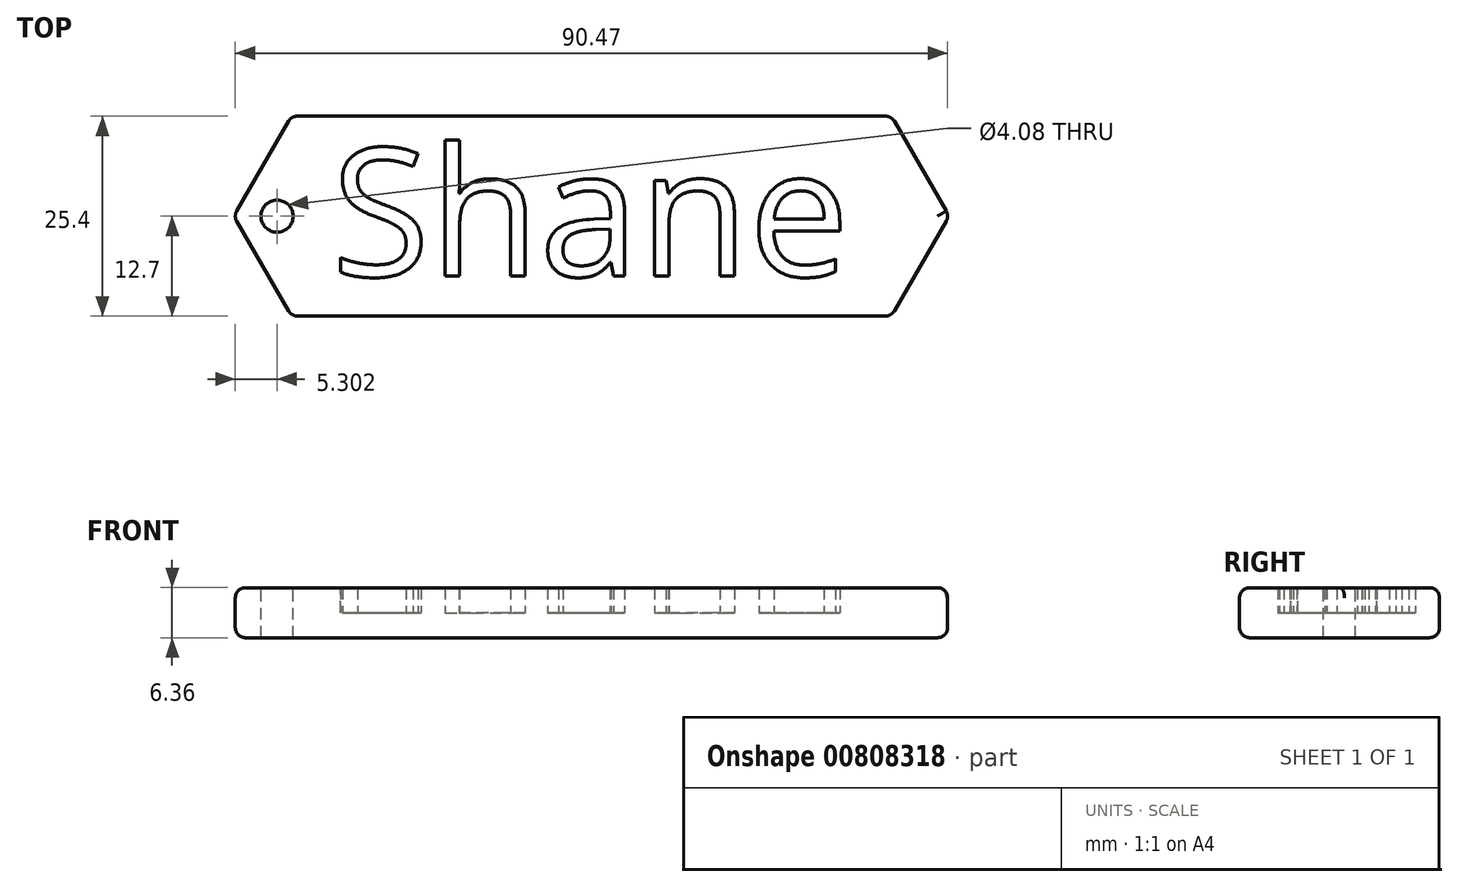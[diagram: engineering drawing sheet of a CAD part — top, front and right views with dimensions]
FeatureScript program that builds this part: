
annotation { "Feature Type Name" : "Feature", "Feature Type Description" : "" }
export const myFeature = defineFeature(function(context is Context, id is Id, definition is map)
    precondition{}
    {
        {
            var Q0;
            Q0=qCreatedBy(makeId("Top.planeOp"),FACE);
            var sketch = newSketch(context, id + "F0", { "sketchPlane" : qUnion([Q0])});
            skLineSegment(sketch, "E0.bottom", {"start": v(-34.81, 12.7) * mm, "end": v(41.39, 12.7) * mm});
            skPoint(sketch, "E0.middle", {"position": v(0, 0) * mm});
            skLineSegment(sketch, "E1", {"start": v(-34.81, -12.7) * mm, "end": v(41.39, -12.7) * mm});
            skLineSegment(sketch, "E2", {"start": v(-34.81, 12.7) * mm, "end": v(-42.15, 0) * mm});
            skLineSegment(sketch, "E3", {"start": v(-42.15, 0) * mm, "end": v(-34.81, -12.7) * mm});
            skLineSegment(sketch, "E4", {"start": v(41.39, 12.7) * mm, "end": v(48.72, 0) * mm});
            skLineSegment(sketch, "E5", {"start": v(48.72, 0) * mm, "end": v(41.39, -12.7) * mm});
            skSolve(sketch);
        }
        {
            var Q0;
            Q0=makeQuery(id+"F0.imprint","IMPRINT",FACE,{"disambiguationData":[TD([[makeQuery(id+"F0.imprint","IMPRINT",EDGE,{"derivedFrom":sQuery(id+"F0.wireOp",EDGE,"E0.bottom")}),-1.0]])]});
            extrude(context, id + "F1", {"entities" : qUnion([Q0]), "endBound" : BoundingType.SYMMETRIC, "depth" : 6.35 * mm, "offsetDistance" : 25.4 * mm});
        }
        {
            var Q0;
            Q0=qCreatedBy(makeId("Top.planeOp"),FACE);
            var sketch = newSketch(context, id + "F2", { "sketchPlane" : qUnion([Q0])});
            skText(sketch, "E6", { "text": "Shane", "fontName": "OpenSans-Regular.ttf"});
            const initialGuessF2  = {"E6": [-0.02973, -0.00762, 1, 0, 0.01636]};
            skSetInitialGuess(sketch, initialGuessF2);
            skSolve(sketch);
        }
        {
            var Q0;
            Q0 = qSketchRegion(id + "F2", true);
            extrude(context, id + "F3", {"entities" : qUnion([Q0]), "operationType" : NewBodyOperationType.REMOVE, "depth" : 5.08 * mm, "offsetDistance" : 25.4 * mm});
        }
        {
            var Q0;
            Q0=qCreatedBy(makeId("Top.planeOp"),FACE);
            var sketch = newSketch(context, id + "F4", { "sketchPlane" : qUnion([Q0])});
            skCircle(sketch, "E7", {"center": v(-36.65, 0) * mm, "radius": 2.04 * mm});
            skSolve(sketch);
        }
        {
            var Q0;
            Q0 = qSketchRegion(id + "F4", true);
            extrude(context, id + "F5", {"entities" : qUnion([Q0]), "operationType" : NewBodyOperationType.REMOVE, "endBound" : BoundingType.THROUGH_ALL, "oppositeDirection" : true, "depth" : 25.4 * mm, "offsetDistance" : 25.4 * mm, "hasSecondDirection" : true, "secondDirectionBound" : SecondDirectionBoundingType.THROUGH_ALL, "secondDirectionOppositeDirection" : false, "secondDirectionDepth" : 25.4 * mm});
        }
        {
            var Q0;
            Q0=makeQuery(id+"F1.opExtrude","CAP_EDGE",EDGE,{"disambiguationData":[OSD([sQuery(id+"F0.wireOp",EDGE,"E0.bottom")])],"isStart":false});
            var Q1;
            Q1=makeQuery(id+"F1.opExtrude","CAP_EDGE",EDGE,{"disambiguationData":[OSD([sQuery(id+"F0.wireOp",EDGE,"E2")])],"isStart":false});
            var Q2;
            Q2=makeQuery(id+"F1.opExtrude","CAP_EDGE",EDGE,{"disambiguationData":[OSD([sQuery(id+"F0.wireOp",EDGE,"E3")])],"isStart":false});
            var Q3;
            Q3=makeQuery(id+"F1.opExtrude","CAP_EDGE",EDGE,{"disambiguationData":[OSD([sQuery(id+"F0.wireOp",EDGE,"E1")])],"isStart":false});
            var Q4;
            Q4=makeQuery(id+"F1.opExtrude","CAP_EDGE",EDGE,{"disambiguationData":[OSD([sQuery(id+"F0.wireOp",EDGE,"E5")])],"isStart":false});
            var Q5;
            Q5=makeQuery(id+"F1.opExtrude","CAP_EDGE",EDGE,{"disambiguationData":[OSD([sQuery(id+"F0.wireOp",EDGE,"E4")])],"isStart":false});
            var Q6;
            Q6=makeQuery(id+"F1.opExtrude","CAP_EDGE",EDGE,{"disambiguationData":[OSD([sQuery(id+"F0.wireOp",EDGE,"E4")])],"isStart":true});
            var Q7;
            Q7=makeQuery(id+"F1.opExtrude","CAP_EDGE",EDGE,{"disambiguationData":[OSD([sQuery(id+"F0.wireOp",EDGE,"E5")])],"isStart":true});
            var Q8;
            Q8=makeQuery(id+"F1.opExtrude","CAP_EDGE",EDGE,{"disambiguationData":[OSD([sQuery(id+"F0.wireOp",EDGE,"E0.bottom")])],"isStart":true});
            var Q9;
            Q9=makeQuery(id+"F1.opExtrude","CAP_EDGE",EDGE,{"disambiguationData":[OSD([sQuery(id+"F0.wireOp",EDGE,"E2")])],"isStart":true});
            var Q10;
            Q10=makeQuery(id+"F1.opExtrude","CAP_EDGE",EDGE,{"disambiguationData":[OSD([sQuery(id+"F0.wireOp",EDGE,"E1")])],"isStart":true});
            var Q11;
            Q11=makeQuery(id+"F1.opExtrude","CAP_EDGE",EDGE,{"disambiguationData":[OSD([sQuery(id+"F0.wireOp",EDGE,"E3")])],"isStart":true});
            var Q12;
            Q12=makeQuery(id+"F1.opExtrude","SWEPT_EDGE",EDGE,{"disambiguationData":[OSD([sQuery(id+"F0.wireOp",EDGE,"E2"),sQuery(id+"F0.wireOp",EDGE,"E3")])]});
            var Q13;
            Q13=makeQuery(id+"F1.opExtrude","SWEPT_EDGE",EDGE,{"disambiguationData":[OSD([sQuery(id+"F0.wireOp",EDGE,"E4"),sQuery(id+"F0.wireOp",EDGE,"E5")])]});
            var Q14;
            Q14=makeQuery(id+"F1.opExtrude","SWEPT_EDGE",EDGE,{"disambiguationData":[OSD([sQuery(id+"F0.wireOp",EDGE,"E0.bottom"),sQuery(id+"F0.wireOp",EDGE,"E4")])]});
            var Q15;
            Q15=makeQuery(id+"F1.opExtrude","SWEPT_EDGE",EDGE,{"disambiguationData":[OSD([sQuery(id+"F0.wireOp",EDGE,"E1"),sQuery(id+"F0.wireOp",EDGE,"E5")])]});
            var Q16;
            Q16=makeQuery(id+"F1.opExtrude","SWEPT_EDGE",EDGE,{"disambiguationData":[OSD([sQuery(id+"F0.wireOp",EDGE,"E1"),sQuery(id+"F0.wireOp",EDGE,"E3")])]});
            var Q17;
            Q17=makeQuery(id+"F1.opExtrude","SWEPT_EDGE",EDGE,{"disambiguationData":[OSD([sQuery(id+"F0.wireOp",EDGE,"E0.bottom"),sQuery(id+"F0.wireOp",EDGE,"E2")])]});
            fillet(context, id + "F6", {"entities" : qUnion([Q0, Q1, Q2, Q3, Q4, Q5, Q6, Q7, Q8, Q9, Q10, Q11, Q12, Q13, Q14, Q15, Q16, Q17]), "radius" : 1.27 * mm, "tangentPropagation" : true, "allowEdgeOverflow" : false});
        }
    });
